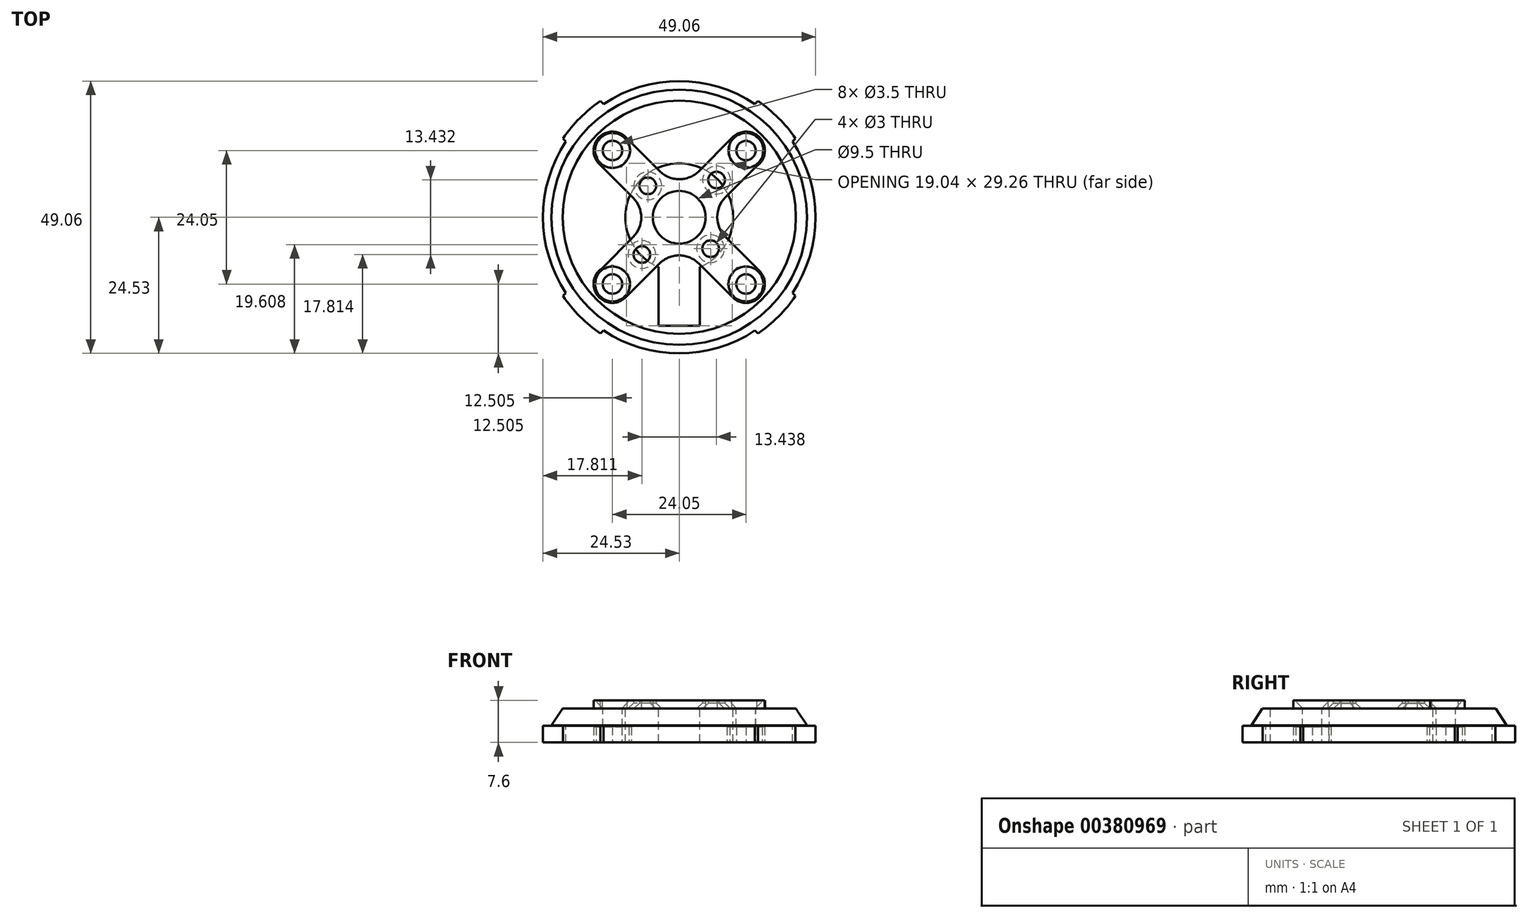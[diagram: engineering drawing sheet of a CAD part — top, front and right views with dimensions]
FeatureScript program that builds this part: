
annotation { "Feature Type Name" : "Feature", "Feature Type Description" : "" }
export const myFeature = defineFeature(function(context is Context, id is Id, definition is map)
    precondition{}
    {
        {
            var Q0;
            Q0=qCreatedBy(makeId("Top.planeOp"),FACE);
            var sketch = newSketch(context, id + "F0", { "sketchPlane" : qUnion([Q0])});
            skCircle(sketch, "E0", {"center": v(0, 0) * mm, "radius": 24.53 * mm});
            skSolve(sketch);
        }
        {
            var Q0;
            Q0 = qSketchRegion(id + "F0", true);
            extrude(context, id + "F1", {"entities" : qUnion([Q0]), "oppositeDirection" : true, "depth" : 3 * mm});
        }
        {
            var Q0;
            Q0=makeQuery(id+"F1.opExtrude","CAP_FACE",FACE,{"disambiguationData":[OSD([sQuery(id+"F0.wireOp",EDGE,"E0")])],"isStart":true});
            var sketch = newSketch(context, id + "F2", { "sketchPlane" : qUnion([Q0])});
            skCircle(sketch, "E1", {"center": v(0, 0) * mm, "radius": 23 * mm});
            skSolve(sketch);
        }
        {
            var Q0;
            Q0 = qSketchRegion(id + "F2", true);
            extrude(context, id + "F3", {"entities" : qUnion([Q0]), "operationType" : NewBodyOperationType.ADD, "depth" : 3.1 * mm});
        }
        {
            var Q0;
            Q0=makeQuery(id+"F3.opExtrude","CAP_EDGE",EDGE,{"disambiguationData":[OSD([sQuery(id+"F2.wireOp",EDGE,"E1")])],"isStart":false});
            chamfer(context, id + "F4", {"entities" : qUnion([Q0]), "chamferType" : ChamferType.TWO_OFFSETS, "width1" : 2 * mm, "oppositeDirection" : false, "width2" : 3 * mm, "tangentPropagation" : true});
        }
        {
            var Q0;
            Q0=makeQuery(id+"F3.opExtrude","CAP_FACE",FACE,{"disambiguationData":[OSD([sQuery(id+"F2.wireOp",EDGE,"E1")])],"isStart":false});
            var sketch = newSketch(context, id + "F5", { "sketchPlane" : qUnion([Q0])});
            skLineSegment(sketch, "E2.bottom", {"start": v(-12.02, 12.02) * mm, "end": v(12.02, 12.02) * mm, "construction": true});
            skLineSegment(sketch, "E2.top", {"start": v(-12.02, -12.02) * mm, "end": v(12.02, -12.02) * mm, "construction": true});
            skLineSegment(sketch, "E2.left", {"start": v(-12.02, 12.02) * mm, "end": v(-12.02, -12.02) * mm, "construction": true});
            skLineSegment(sketch, "E2.right", {"start": v(12.02, 12.02) * mm, "end": v(12.02, -12.02) * mm, "construction": true});
            skPoint(sketch, "E2.middle", {"position": v(0, 0) * mm});
            skCircle(sketch, "E3", {"center": v(-12.02, 12.02) * mm, "radius": 1.75 * mm});
            skCircle(sketch, "E4.1.0", {"center": v(-12.02, -12.02) * mm, "radius": 1.75 * mm});
            skCircle(sketch, "E4.2.0", {"center": v(12.02, -12.02) * mm, "radius": 1.75 * mm});
            skCircle(sketch, "E4.3.0", {"center": v(12.02, 12.02) * mm, "radius": 1.75 * mm});
            skSolve(sketch);
        }
        {
            var Q0;
            Q0=makeQuery(id+"F5.imprint","IMPRINT",FACE,{"disambiguationData":[TD([[makeQuery(id+"F5.imprint","IMPRINT",EDGE,{"derivedFrom":sQuery(id+"F5.wireOp",EDGE,"E3")}),-1.0]])]});
            var sketch = newSketch(context, id + "F6", { "sketchPlane" : qUnion([Q0])});
            skArc(sketch, "E5", {"start": v(3.71, -8.97) * mm, "mid": v(0, 9.7) * mm, "end": v(-3.71, -8.97) * mm});
            skLineSegment(sketch, "E6.top", {"start": v(-3.71, -19.55) * mm, "end": v(3.71, -19.55) * mm});
            skLineSegment(sketch, "E6.left", {"start": v(-3.71, -8.97) * mm, "end": v(-3.71, -19.55) * mm});
            skLineSegment(sketch, "E6.right", {"start": v(3.71, -8.97) * mm, "end": v(3.71, -19.55) * mm});
            skSolve(sketch);
        }
        {
            var Q0;
            Q0 = qSketchRegion(id + "F6", true);
            extrude(context, id + "F7", {"entities" : qUnion([Q0]), "operationType" : NewBodyOperationType.REMOVE, "oppositeDirection" : true, "depth" : 25 * mm});
        }
        {
            var Q0;
            Q0 = qSketchRegion(id + "F5", true);
            extrude(context, id + "F8", {"entities" : qUnion([Q0]), "operationType" : NewBodyOperationType.REMOVE, "oppositeDirection" : true, "depth" : 25 * mm});
        }
        {
            var Q0;
            Q0=makeQuery(id+"F3.opExtrude","CAP_FACE",FACE,{"disambiguationData":[OSD([sQuery(id+"F2.wireOp",EDGE,"E1")])],"isStart":false});
            var sketch = newSketch(context, id + "F9", { "sketchPlane" : qUnion([Q0])});
            skArc(sketch, "E7", {"start": v(-9.44, 14.24) * mm, "mid": v(-14.4, 14.46) * mm, "end": v(-14.3, 9.5) * mm});
            skArc(sketch, "E8.1.0", {"start": v(-13.89, -9.17) * mm, "mid": v(-14.66, -14.17) * mm, "end": v(-9.62, -14.42) * mm});
            skArc(sketch, "E8.2.0", {"start": v(9.61, -14.43) * mm, "mid": v(14.42, -14.43) * mm, "end": v(14.42, -9.62) * mm});
            skArc(sketch, "E8.3.0", {"start": v(13.94, 9.2) * mm, "mid": v(14.56, 14.28) * mm, "end": v(9.45, 14.24) * mm});
            skPoint(sketch, "E8.center", {"position": v(0, 0) * mm});
            skLineSegment(sketch, "E9", {"start": v(-14.3, 9.5) * mm, "end": v(-8.3, 3.5) * mm});
            skLineSegment(sketch, "E10", {"start": v(-9.8, 14.6) * mm, "end": v(-3.52, 8.32) * mm});
            skLineSegment(sketch, "E11", {"start": v(13.94, 9.2) * mm, "end": v(8.3, 3.56) * mm});
            skLineSegment(sketch, "E12", {"start": v(9.8, 14.59) * mm, "end": v(3.56, 8.33) * mm});
            skLineSegment(sketch, "E13.trimOffspring", {"start": v(-8.3, -3.56) * mm, "end": v(-13.89, -9.17) * mm});
            skLineSegment(sketch, "E14.trimOffspring", {"start": v(3.52, -8.33) * mm, "end": v(9.61, -14.43) * mm});
            skLineSegment(sketch, "E15.trimOffspring", {"start": v(-3.55, -8.34) * mm, "end": v(-9.62, -14.42) * mm});
            skLineSegment(sketch, "E16.trimOffspring", {"start": v(8.31, -3.5) * mm, "end": v(14.42, -9.62) * mm});
            skCircle(sketch, "E17", {"center": v(-12.02, 12.02) * mm, "radius": 1.75 * mm});
            skCircle(sketch, "E18.1.0", {"center": v(-12.02, -12.02) * mm, "radius": 1.75 * mm});
            skCircle(sketch, "E18.2.0", {"center": v(12.02, -12.02) * mm, "radius": 1.75 * mm});
            skCircle(sketch, "E18.3.0", {"center": v(12.02, 12.02) * mm, "radius": 1.75 * mm});
            skCircle(sketch, "E19", {"center": v(0, 0) * mm, "radius": 4.75 * mm});
            skPoint(sketch, "E20.visualSharp", {"position": v(-4.77, -0.03) * mm});
            skArc(sketch, "E20.filletArc", {"start": v(-8.3, -3.56) * mm, "mid": v(-6.84, -0.03) * mm, "end": v(-8.3, 3.5) * mm});
            skPoint(sketch, "E21.visualSharp", {"position": v(4.78, 0.02) * mm});
            skArc(sketch, "E21.filletArc", {"start": v(8.3, 3.56) * mm, "mid": v(6.85, 0.02) * mm, "end": v(8.31, -3.5) * mm});
            skPoint(sketch, "E22.visualSharp", {"position": v(0.02, 4.78) * mm});
            skArc(sketch, "E22.filletArc", {"start": v(-3.52, 8.32) * mm, "mid": v(0.02, 6.86) * mm, "end": v(3.56, 8.33) * mm});
            skPoint(sketch, "E23.visualSharp", {"position": v(-0.02, -4.79) * mm});
            skArc(sketch, "E23.filletArc", {"start": v(3.52, -8.33) * mm, "mid": v(-0.02, -6.87) * mm, "end": v(-3.55, -8.34) * mm});
            skLineSegment(sketch, "E24", {"start": v(0, 0) * mm, "end": v(-12.02, 12.02) * mm, "construction": true});
            skCircle(sketch, "E25", {"center": v(-5.66, 5.66) * mm, "radius": 1.5 * mm});
            skLineSegment(sketch, "E26", {"start": v(0, 0) * mm, "end": v(12.02, -12.02) * mm, "construction": true});
            skLineSegment(sketch, "E27", {"start": v(0, 0) * mm, "end": v(-12.02, -12.02) * mm, "construction": true});
            skLineSegment(sketch, "E28", {"start": v(0, 0) * mm, "end": v(12.02, 12.02) * mm, "construction": true});
            skCircle(sketch, "E29", {"center": v(5.66, -5.66) * mm, "radius": 1.5 * mm});
            skCircle(sketch, "E30", {"center": v(-6.72, -6.72) * mm, "radius": 1.5 * mm});
            skCircle(sketch, "E31", {"center": v(6.72, 6.72) * mm, "radius": 1.5 * mm});
            skSolve(sketch);
        }
        {
            var Q0;
            Q0 = qSketchRegion(id + "F9", true);
            extrude(context, id + "F10", {"entities" : qUnion([Q0]), "depth" : 1.5 * mm});
        }
        {
            var Q0;
            Q0=makeQuery(id+"F10.opExtrude","CAP_EDGE",EDGE,{"disambiguationData":[OSD([sQuery(id+"F9.wireOp",EDGE,"E17")])],"isStart":false});
            var Q1;
            Q1=makeQuery(id+"F10.opExtrude","CAP_EDGE",EDGE,{"disambiguationData":[OSD([sQuery(id+"F9.wireOp",EDGE,"E18.3.0")])],"isStart":false});
            var Q2;
            Q2=makeQuery(id+"F10.opExtrude","CAP_EDGE",EDGE,{"disambiguationData":[OSD([sQuery(id+"F9.wireOp",EDGE,"E18.1.0")])],"isStart":false});
            var Q3;
            Q3=makeQuery(id+"F10.opExtrude","CAP_EDGE",EDGE,{"disambiguationData":[OSD([sQuery(id+"F9.wireOp",EDGE,"E18.2.0")])],"isStart":false});
            chamfer(context, id + "F11", {"entities" : qUnion([Q0, Q1, Q2, Q3]), "width" : 1.4 * mm, "tangentPropagation" : true});
        }
        {
            var Q0;
            Q0=makeQuery(id+"F1.opExtrude","CAP_FACE",FACE,{"disambiguationData":[OSD([sQuery(id+"F0.wireOp",EDGE,"E0")])],"isStart":false});
            var sketch = newSketch(context, id + "F12", { "sketchPlane" : qUnion([Q0])});
            skCircle(sketch, "E32.cCircle", {"center": v(12.02, 12.02) * mm, "radius": 2.94 * mm, "construction": true});
            skLineSegment(sketch, "E32.0", {"start": v(13.72, 9.08) * mm, "end": v(10.32, 9.08) * mm});
            skLineSegment(sketch, "E32.1", {"start": v(10.32, 9.08) * mm, "end": v(8.62, 12.02) * mm});
            skLineSegment(sketch, "E32.2", {"start": v(8.62, 12.02) * mm, "end": v(10.32, 14.97) * mm});
            skLineSegment(sketch, "E32.3", {"start": v(10.32, 14.97) * mm, "end": v(13.72, 14.97) * mm});
            skLineSegment(sketch, "E32.4", {"start": v(13.72, 14.97) * mm, "end": v(15.42, 12.02) * mm});
            skLineSegment(sketch, "E32.5", {"start": v(15.42, 12.02) * mm, "end": v(13.72, 9.08) * mm});
            skPoint(sketch, "E32.0.midPoint", {"position": v(12.02, 9.08) * mm});
            skLineSegment(sketch, "E33.1.0", {"start": v(-12.02, 8.62) * mm, "end": v(-14.97, 10.32) * mm});
            skLineSegment(sketch, "E33.1.1", {"start": v(-14.97, 10.32) * mm, "end": v(-14.97, 13.72) * mm});
            skLineSegment(sketch, "E33.1.2", {"start": v(-14.97, 13.72) * mm, "end": v(-12.02, 15.42) * mm});
            skLineSegment(sketch, "E33.1.3", {"start": v(-12.02, 15.42) * mm, "end": v(-9.08, 13.72) * mm});
            skLineSegment(sketch, "E33.1.4", {"start": v(-9.08, 13.72) * mm, "end": v(-9.08, 10.32) * mm});
            skLineSegment(sketch, "E33.1.5", {"start": v(-9.08, 10.32) * mm, "end": v(-12.02, 8.62) * mm});
            skLineSegment(sketch, "E33.2.0", {"start": v(-8.62, -12.02) * mm, "end": v(-10.32, -14.97) * mm});
            skLineSegment(sketch, "E33.2.1", {"start": v(-10.32, -14.97) * mm, "end": v(-13.72, -14.97) * mm});
            skLineSegment(sketch, "E33.2.2", {"start": v(-13.72, -14.97) * mm, "end": v(-15.42, -12.02) * mm});
            skLineSegment(sketch, "E33.2.3", {"start": v(-15.42, -12.02) * mm, "end": v(-13.72, -9.08) * mm});
            skLineSegment(sketch, "E33.2.4", {"start": v(-13.72, -9.08) * mm, "end": v(-10.32, -9.08) * mm});
            skLineSegment(sketch, "E33.2.5", {"start": v(-10.32, -9.08) * mm, "end": v(-8.62, -12.02) * mm});
            skLineSegment(sketch, "E33.3.0", {"start": v(12.02, -8.62) * mm, "end": v(14.97, -10.32) * mm});
            skLineSegment(sketch, "E33.3.1", {"start": v(14.97, -10.32) * mm, "end": v(14.97, -13.72) * mm});
            skLineSegment(sketch, "E33.3.2", {"start": v(14.97, -13.72) * mm, "end": v(12.02, -15.42) * mm});
            skLineSegment(sketch, "E33.3.3", {"start": v(12.02, -15.42) * mm, "end": v(9.08, -13.72) * mm});
            skLineSegment(sketch, "E33.3.4", {"start": v(9.08, -13.72) * mm, "end": v(9.08, -10.32) * mm});
            skLineSegment(sketch, "E33.3.5", {"start": v(9.08, -10.32) * mm, "end": v(12.02, -8.62) * mm});
            skPoint(sketch, "E33.center", {"position": v(0, 0) * mm});
            skSolve(sketch);
        }
        {
            var Q0;
            Q0 = qSketchRegion(id + "F12", true);
            extrude(context, id + "F13", {"entities" : qUnion([Q0]), "operationType" : NewBodyOperationType.REMOVE, "oppositeDirection" : true, "depth" : 2.8 * mm});
        }
        {
            var Q0;
            Q0=makeQuery(id+"F1.opExtrude","CAP_FACE",FACE,{"disambiguationData":[OSD([sQuery(id+"F0.wireOp",EDGE,"E0")])],"isStart":true});
            var sketch = newSketch(context, id + "F14", { "sketchPlane" : qUnion([Q0])});
            skArc(sketch, "E34.0", {"start": v(-20.93, -14.18) * mm, "mid": v(-17.88, -17.88) * mm, "end": v(-14.18, -20.93) * mm});
            skLineSegment(sketch, "E35.left", {"start": v(-14.18, 20.93) * mm, "end": v(0, 6.75) * mm});
            skLineSegment(sketch, "E35.right", {"start": v(-20.93, 14.18) * mm, "end": v(-6.75, 0) * mm});
            skLineSegment(sketch, "E36.MirrorCS", {"start": v(14.18, 20.93) * mm, "end": v(0, 6.75) * mm});
            skLineSegment(sketch, "E37.MirrorCS", {"start": v(20.93, 14.18) * mm, "end": v(6.75, 0) * mm});
            skLineSegment(sketch, "E38.trimOffspring", {"start": v(-6.75, 0) * mm, "end": v(-20.93, -14.18) * mm});
            skLineSegment(sketch, "E39.trimOffspring", {"start": v(0, -6.75) * mm, "end": v(14.18, -20.93) * mm});
            skLineSegment(sketch, "E40.trimOffspring", {"start": v(0, -6.75) * mm, "end": v(-14.18, -20.93) * mm});
            skLineSegment(sketch, "E41.trimOffspring", {"start": v(6.75, 0) * mm, "end": v(20.93, -14.18) * mm});
            skPoint(sketch, "E35.bottom.end.orphan", {"position": v(-22.7, 15.96) * mm});
            skArc(sketch, "E42.trimOffspring", {"start": v(14.18, -20.93) * mm, "mid": v(17.88, -17.88) * mm, "end": v(20.93, -14.18) * mm});
            skPoint(sketch, "E35.top.end.orphan", {"position": v(15.96, -22.7) * mm});
            skPoint(sketch, "E43.orphan", {"position": v(22.7, -15.96) * mm});
            skPoint(sketch, "E44.orphan", {"position": v(-15.96, 22.7) * mm});
            skArc(sketch, "E45.trimOffspring", {"start": v(-14.18, 20.93) * mm, "mid": v(-17.88, 17.88) * mm, "end": v(-20.93, 14.18) * mm});
            skArc(sketch, "E46.trimOffspring", {"start": v(20.93, 14.18) * mm, "mid": v(17.88, 17.88) * mm, "end": v(14.18, 20.93) * mm});
            skSolve(sketch);
        }
        {
            var Q0;
            {var subQ0=sQuery(id+"F14.wireOp",EDGE,"E45.trimOffspring");Q0=makeQuery(id+"F14.imprint","IMPRINT",FACE,{"disambiguationData":[TD([[makeQuery(id+"F14.imprint","IMPRINT",EDGE,{"derivedFrom":subQ0}),1.0]])]});}
            var Q1;
            {var subQ0=sQuery(id+"F14.wireOp",EDGE,"E46.trimOffspring");Q1=makeQuery(id+"F14.imprint","IMPRINT",FACE,{"disambiguationData":[TD([[makeQuery(id+"F14.imprint","IMPRINT",EDGE,{"derivedFrom":subQ0}),1.0]])]});}
            var Q2;
            {var subQ0=sQuery(id+"F14.wireOp",EDGE,"E34.0");Q2=makeQuery(id+"F14.imprint","IMPRINT",FACE,{"disambiguationData":[TD([[makeQuery(id+"F14.imprint","IMPRINT",EDGE,{"derivedFrom":subQ0}),1.0]])]});}
            var Q3;
            {var subQ0=sQuery(id+"F14.wireOp",EDGE,"E42.trimOffspring");Q3=makeQuery(id+"F14.imprint","IMPRINT",FACE,{"disambiguationData":[TD([[makeQuery(id+"F14.imprint","IMPRINT",EDGE,{"derivedFrom":subQ0}),1.0]])]});}
            var Q4;
            Q4=makeQuery(id+"F1.opExtrude","CAP_FACE",FACE,{"disambiguationData":[OSD([sQuery(id+"F0.wireOp",EDGE,"E0")])],"isStart":false});
            extrude(context, id + "F15", {"entities" : qUnion([Q0, Q1, Q2, Q3]), "operationType" : NewBodyOperationType.ADD, "endBound" : BoundingType.UP_TO_SURFACE, "oppositeDirection" : true, "endBoundEntityFace" : qUnion([Q4]), "depth" : 25 * mm});
        }
        {
            var Q0;
            Q0=makeQuery(id+"F10.opExtrude","CAP_EDGE",EDGE,{"disambiguationData":[OSD([sQuery(id+"F9.wireOp",EDGE,"E30")])],"isStart":true});
            var Q1;
            Q1=makeQuery(id+"F10.opExtrude","CAP_EDGE",EDGE,{"disambiguationData":[OSD([sQuery(id+"F9.wireOp",EDGE,"E25")])],"isStart":true});
            var Q2;
            Q2=makeQuery(id+"F10.opExtrude","CAP_EDGE",EDGE,{"disambiguationData":[OSD([sQuery(id+"F9.wireOp",EDGE,"E29")])],"isStart":true});
            var Q3;
            Q3=makeQuery(id+"F10.opExtrude","CAP_EDGE",EDGE,{"disambiguationData":[OSD([sQuery(id+"F9.wireOp",EDGE,"E31")])],"isStart":true});
            chamfer(context, id + "F16", {"entities" : qUnion([Q0, Q1, Q2, Q3]), "width" : 1 * mm, "tangentPropagation" : true});
        }
    });
